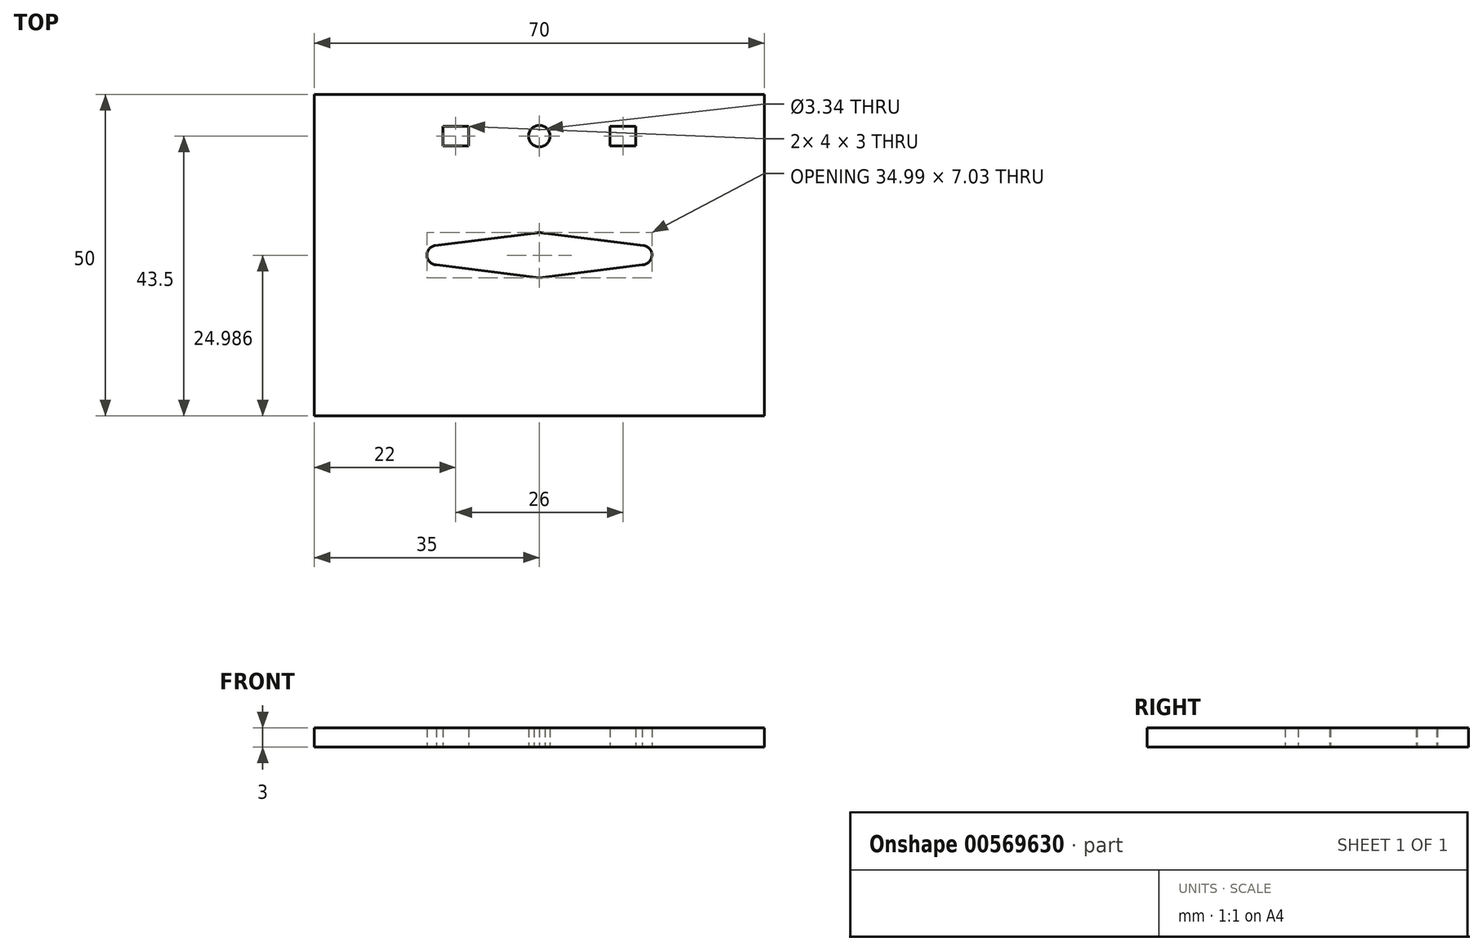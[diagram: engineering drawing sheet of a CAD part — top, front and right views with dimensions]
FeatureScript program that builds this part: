
annotation { "Feature Type Name" : "Feature", "Feature Type Description" : "" }
export const myFeature = defineFeature(function(context is Context, id is Id, definition is map)
    precondition{}
    {
        {
            var Q0;
            Q0=qCreatedBy(makeId("Top.planeOp"),FACE);
            var sketch = newSketch(context, id + "F0", { "sketchPlane" : qUnion([Q0])});
            skLineSegment(sketch, "E0.bottom", {"start": v(-35, 25) * mm, "end": v(35, 25) * mm});
            skLineSegment(sketch, "E0.top", {"start": v(-35, -25) * mm, "end": v(35, -25) * mm});
            skLineSegment(sketch, "E0.left", {"start": v(-35, 25) * mm, "end": v(-35, -25) * mm});
            skLineSegment(sketch, "E0.right", {"start": v(35, 25) * mm, "end": v(35, -25) * mm});
            skLineSegment(sketch, "E1.bottom", {"start": v(11, 20) * mm, "end": v(15, 20) * mm});
            skLineSegment(sketch, "E1.top", {"start": v(11, 17) * mm, "end": v(15, 17) * mm});
            skLineSegment(sketch, "E1.left", {"start": v(11, 20) * mm, "end": v(11, 17) * mm});
            skLineSegment(sketch, "E1.right", {"start": v(15, 20) * mm, "end": v(15, 17) * mm});
            skLineSegment(sketch, "E2", {"start": v(-45.38, 0) * mm, "end": v(42.75, 0) * mm, "construction": true});
            skLineSegment(sketch, "E3.MirrorCS", {"start": v(-11, 17) * mm, "end": v(-15, 17) * mm});
            skLineSegment(sketch, "E4.MirrorCS", {"start": v(-15, 20) * mm, "end": v(-15, 17) * mm});
            skLineSegment(sketch, "E5.MirrorCS", {"start": v(-11, 20) * mm, "end": v(-11, 17) * mm});
            skLineSegment(sketch, "E6.MirrorCS", {"start": v(-11, 20) * mm, "end": v(-15, 20) * mm});
            skPoint(sketch, "E7.left.start.orphan", {"position": v(-15, 9.45) * mm});
            skPoint(sketch, "E7.right.end.orphan", {"position": v(-11, 6.45) * mm});
            skPoint(sketch, "E7.right.start.orphan", {"position": v(-11, 9.45) * mm});
            skLineSegment(sketch, "E8", {"start": v(-37.58, 18.5) * mm, "end": v(45.54, 18.5) * mm, "construction": true});
            skCircle(sketch, "E9", {"center": v(0, 18.5) * mm, "radius": 1.67 * mm});
            skPoint(sketch, "E10.center.orphan", {"position": v(0, 7.84) * mm});
            skArc(sketch, "E11", {"start": v(-0.44, -3.47) * mm, "mid": v(0, -3.5) * mm, "end": v(0.44, -3.47) * mm});
            skArc(sketch, "E12", {"start": v(-16.18, 1.49) * mm, "mid": v(-17.5, -0.09) * mm, "end": v(-16.01, -1.5) * mm});
            skLineSegment(sketch, "E13", {"start": v(0, 3.5) * mm, "end": v(-16.18, 1.49) * mm});
            skLineSegment(sketch, "E14", {"start": v(-16.01, -1.5) * mm, "end": v(0, -3.53) * mm});
            skLineSegment(sketch, "E15.MirrorCS", {"start": v(0, 3.5) * mm, "end": v(16.18, 1.49) * mm});
            skLineSegment(sketch, "E16.MirrorCS", {"start": v(16.01, -1.5) * mm, "end": v(0, -3.53) * mm});
            skArc(sketch, "E17.MirrorCS", {"start": v(16.18, 1.49) * mm, "mid": v(17.5, -0.09) * mm, "end": v(16.01, -1.5) * mm});
            skArc(sketch, "E18.trimOffspring", {"start": v(0.86, 3.4) * mm, "mid": v(0, 3.5) * mm, "end": v(-0.86, 3.4) * mm});
            skSolve(sketch);
        }
        {
            var Q0;
            Q0 = qSketchRegion(id + "F0", true);
            extrude(context, id + "F1", {"entities" : qUnion([Q0]), "depth" : 3 * mm, "offsetDistance" : 25 * mm});
        }
    });
